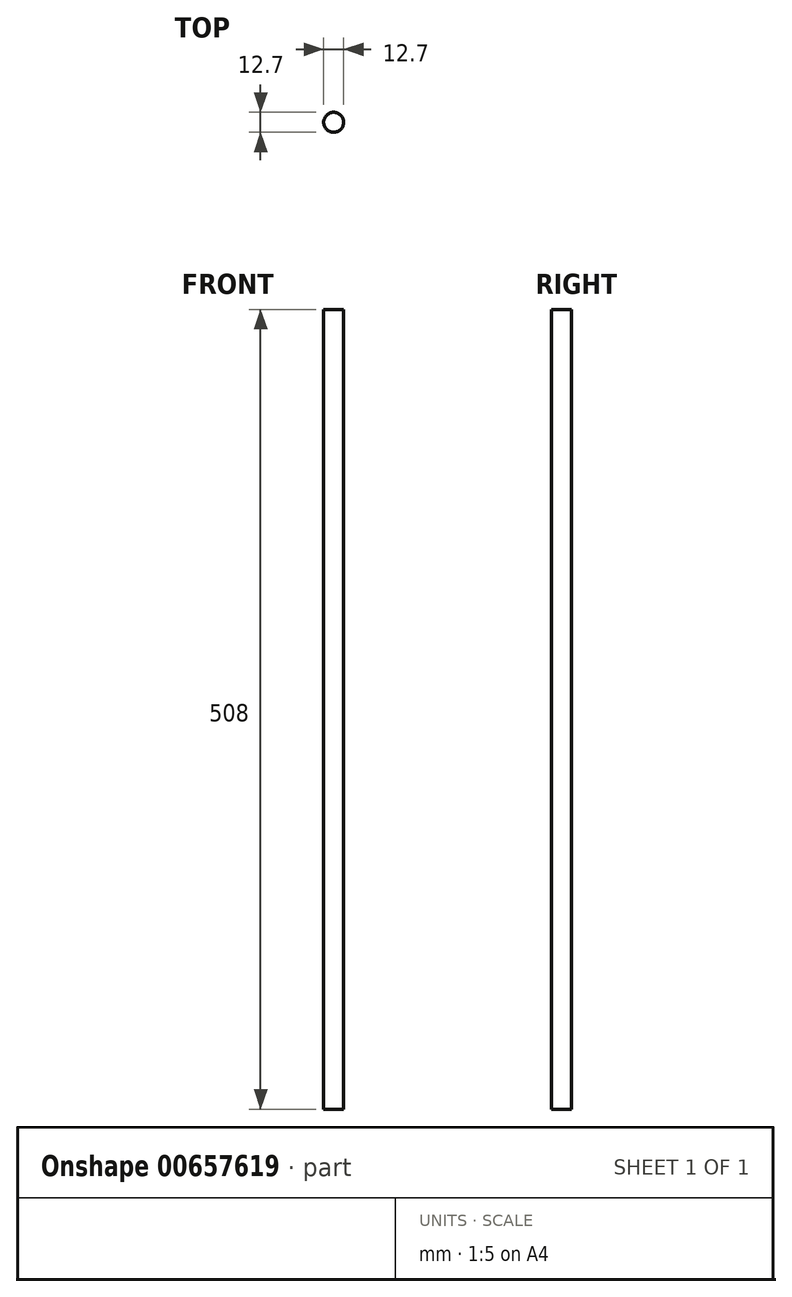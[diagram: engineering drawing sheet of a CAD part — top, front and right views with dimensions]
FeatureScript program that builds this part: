
annotation { "Feature Type Name" : "Feature", "Feature Type Description" : "" }
export const myFeature = defineFeature(function(context is Context, id is Id, definition is map)
    precondition{}
    {
        {
            var Q0;
            Q0=qCreatedBy(makeId("Top.planeOp"),FACE);
            var sketch = newSketch(context, id + "F0", { "sketchPlane" : qUnion([Q0])});
            skCircle(sketch, "E0", {"center": v(0, 0) * mm, "radius": 6.35 * mm});
            skSolve(sketch);
        }
        {
            var Q0;
            Q0=makeQuery(id+"F0.imprint","IMPRINT",FACE,{"disambiguationData":[TD([[makeQuery(id+"F0.imprint","IMPRINT",EDGE,{"derivedFrom":sQuery(id+"F0.wireOp",EDGE,"E0")}),1.0]])]});
            extrude(context, id + "F1", {"entities" : qUnion([Q0]), "depth" : 508 * mm, "offsetDistance" : 25.4 * mm});
        }
    });
